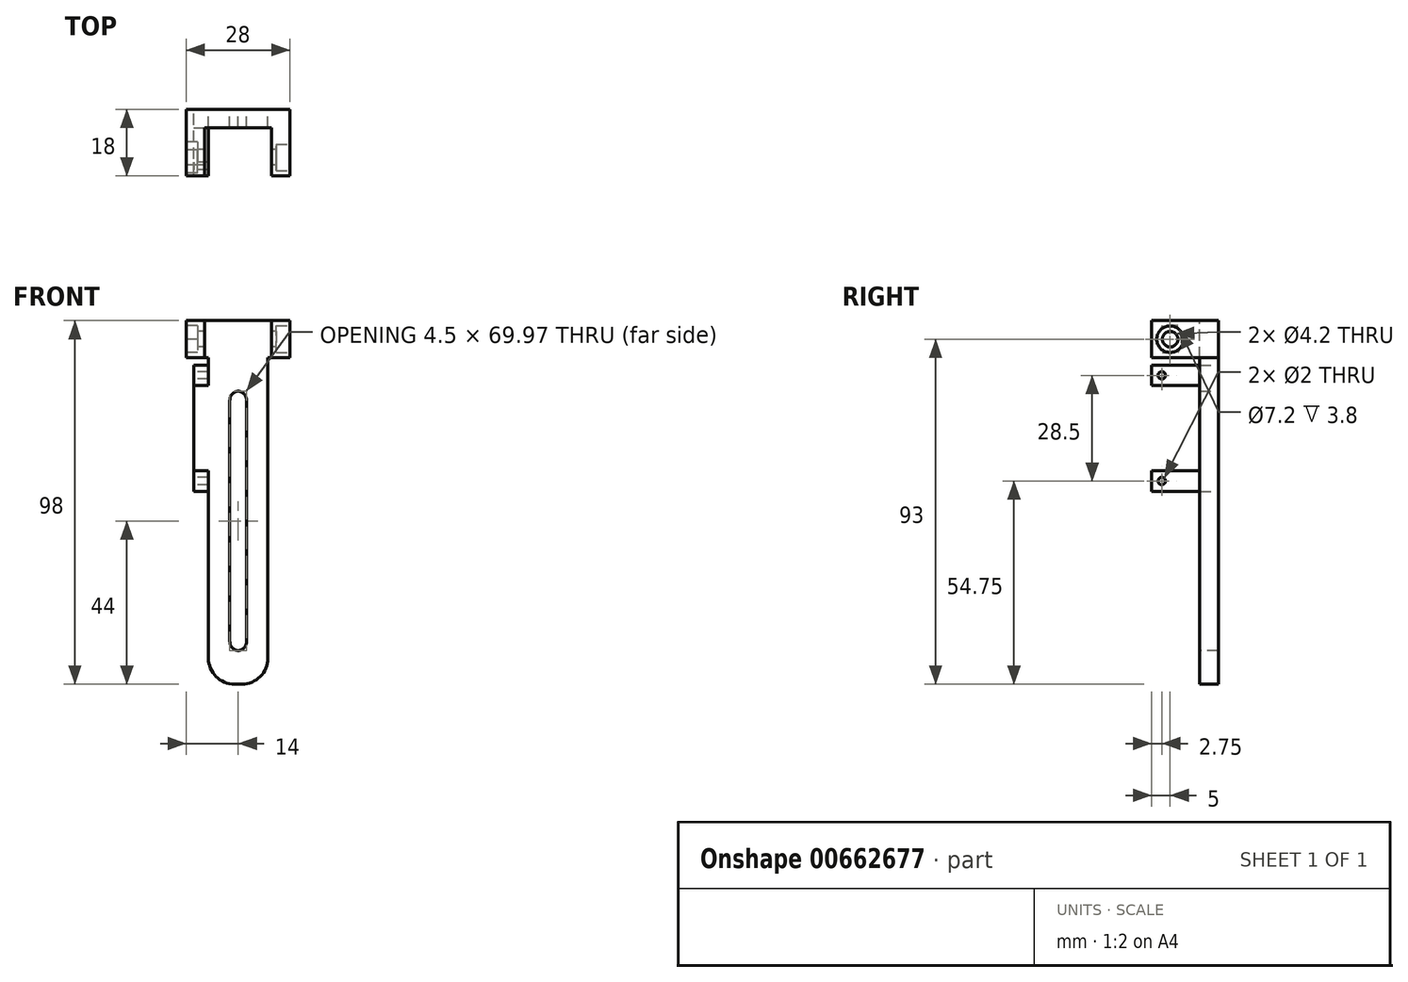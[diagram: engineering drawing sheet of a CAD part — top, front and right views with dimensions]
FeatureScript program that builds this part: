
annotation { "Feature Type Name" : "Feature", "Feature Type Description" : "" }
export const myFeature = defineFeature(function(context is Context, id is Id, definition is map)
    precondition{}
    {
        {
            var Q0;
            Q0=qCreatedBy(makeId("Front.planeOp"),FACE);
            var sketch = newSketch(context, id + "F0", { "sketchPlane" : qUnion([Q0])});
            skLineSegment(sketch, "E0.bottom", {"start": v(8, -44) * mm, "end": v(-8, -44) * mm});
            skLineSegment(sketch, "E0.top", {"start": v(8, 44) * mm, "end": v(-8, 44) * mm});
            skLineSegment(sketch, "E0.left", {"start": v(8, -44) * mm, "end": v(8, 44) * mm});
            skLineSegment(sketch, "E0.right", {"start": v(-8, -44) * mm, "end": v(-8, 44) * mm});
            skPoint(sketch, "E0.middle", {"position": v(0, 0) * mm});
            skLineSegment(sketch, "E1.bottom", {"start": v(-8, 42) * mm, "end": v(-12, 42) * mm});
            skLineSegment(sketch, "E1.top", {"start": v(-8, 8) * mm, "end": v(-12, 8) * mm});
            skLineSegment(sketch, "E1.left", {"start": v(-8, 42) * mm, "end": v(-8, 8) * mm});
            skLineSegment(sketch, "E1.right", {"start": v(-12, 42) * mm, "end": v(-12, 8) * mm});
            skLineSegment(sketch, "E2.bottom", {"start": v(14, 44) * mm, "end": v(8, 44) * mm});
            skLineSegment(sketch, "E2.top", {"start": v(14, 54) * mm, "end": v(-14, 54) * mm});
            skLineSegment(sketch, "E2.left", {"start": v(14, 44) * mm, "end": v(14, 54) * mm});
            skLineSegment(sketch, "E2.right", {"start": v(-14, 44) * mm, "end": v(-14, 54) * mm});
            skLineSegment(sketch, "E3.bottom", {"start": v(2.25, -35) * mm, "end": v(-2.25, -35) * mm});
            skLineSegment(sketch, "E3.top", {"start": v(2.25, 35) * mm, "end": v(-2.25, 35) * mm});
            skLineSegment(sketch, "E3.left", {"start": v(2.25, -35) * mm, "end": v(2.25, 35) * mm});
            skLineSegment(sketch, "E3.right", {"start": v(-2.25, -35) * mm, "end": v(-2.25, 35) * mm});
            skPoint(sketch, "E4", {"position": v(0, 54) * mm});
            skLineSegment(sketch, "E5.trimOffspring", {"start": v(-8, 44) * mm, "end": v(-14, 44) * mm});
            skSolve(sketch);
        }
        {
            var Q0;
            {var subQ1=sQuery(id+"F0.wireOp",EDGE,"E0.bottom");Q0=makeQuery(id+"F0.imprint","IMPRINT",FACE,{"disambiguationData":[TD([[makeQuery(id+"F0.imprint","IMPRINT",EDGE,{"derivedFrom":subQ1}),-1.0]])]});}
            var Q1;
            Q1=makeQuery(id+"F0.imprint","IMPRINT",FACE,{"disambiguationData":[TD([[makeQuery(id+"F0.imprint","IMPRINT",EDGE,{"derivedFrom":sQuery(id+"F0.wireOp",EDGE,"E0.top")}),-1.0]])]});
            var Q2;
            Q2=makeQuery(id+"F0.imprint","IMPRINT",FACE,{"disambiguationData":[TD([[makeQuery(id+"F0.imprint","IMPRINT",EDGE,{"derivedFrom":sQuery(id+"F0.wireOp",EDGE,"E1.bottom")}),1.0]])]});
            extrude(context, id + "F1", {"entities" : qUnion([Q0, Q1, Q2]), "depth" : 5 * mm});
        }
        {
            var Q0;
            Q0=makeQuery(id+"F1.opExtrude","CAP_FACE",FACE,{"disambiguationData":[OSD([sQuery(id+"F0.wireOp",EDGE,"E0.bottom"),sQuery(id+"F0.wireOp",EDGE,"E0.left"),sQuery(id+"F0.wireOp",EDGE,"E0.right"),sQuery(id+"F0.wireOp",EDGE,"E1.bottom"),sQuery(id+"F0.wireOp",EDGE,"E1.top"),sQuery(id+"F0.wireOp",EDGE,"E1.right"),sQuery(id+"F0.wireOp",EDGE,"E2.bottom"),sQuery(id+"F0.wireOp",EDGE,"E2.top"),sQuery(id+"F0.wireOp",EDGE,"E2.left"),sQuery(id+"F0.wireOp",EDGE,"E2.right"),sQuery(id+"F0.wireOp",EDGE,"E3.bottom"),sQuery(id+"F0.wireOp",EDGE,"E3.top"),sQuery(id+"F0.wireOp",EDGE,"E3.left"),sQuery(id+"F0.wireOp",EDGE,"E3.right"),sQuery(id+"F0.wireOp",EDGE,"E5.trimOffspring")])],"isStart":false});
            var sketch = newSketch(context, id + "F2", { "sketchPlane" : qUnion([Q0])});
            skLineSegment(sketch, "E6.bottom", {"start": v(14, 44) * mm, "end": v(9, 44) * mm});
            skLineSegment(sketch, "E6.top", {"start": v(14, 54) * mm, "end": v(9, 54) * mm});
            skLineSegment(sketch, "E6.left", {"start": v(14, 44) * mm, "end": v(14, 54) * mm});
            skLineSegment(sketch, "E6.right", {"start": v(9, 44) * mm, "end": v(9, 54) * mm});
            skLineSegment(sketch, "E7.bottom", {"start": v(-14, 44) * mm, "end": v(-9, 44) * mm});
            skLineSegment(sketch, "E7.top", {"start": v(-14, 54) * mm, "end": v(-9, 54) * mm});
            skLineSegment(sketch, "E7.left", {"start": v(-14, 44) * mm, "end": v(-14, 54) * mm});
            skLineSegment(sketch, "E7.right", {"start": v(-9, 44) * mm, "end": v(-9, 54) * mm});
            skLineSegment(sketch, "E8.bottom", {"start": v(-12, 8) * mm, "end": v(-8, 8) * mm});
            skLineSegment(sketch, "E8.top", {"start": v(-12, 13.5) * mm, "end": v(-8, 13.5) * mm});
            skLineSegment(sketch, "E8.left", {"start": v(-12, 8) * mm, "end": v(-12, 13.5) * mm});
            skLineSegment(sketch, "E8.right", {"start": v(-8, 8) * mm, "end": v(-8, 13.5) * mm});
            skLineSegment(sketch, "E9.bottom", {"start": v(-12, 42) * mm, "end": v(-8, 42) * mm});
            skLineSegment(sketch, "E9.top", {"start": v(-12, 36.5) * mm, "end": v(-8, 36.5) * mm});
            skLineSegment(sketch, "E9.left", {"start": v(-12, 42) * mm, "end": v(-12, 36.5) * mm});
            skLineSegment(sketch, "E9.right", {"start": v(-8, 42) * mm, "end": v(-8, 36.5) * mm});
            skSolve(sketch);
        }
        {
            var Q0;
            Q0=qSketchRegion(id+"F2",true);
            extrude(context, id + "F3", {"entities" : qUnion([Q0]), "operationType" : NewBodyOperationType.ADD, "depth" : 13 * mm});
        }
        {
            var Q0;
            Q0=makeQuery(id+"F3.boolean.opBoolean","MERGE",FACE,{"derivedFrom":[makeQuery(id+"F1.opExtrude","SWEPT_FACE",FACE,{"disambiguationData":[OSD([sQuery(id+"F0.wireOp",EDGE,"E2.right")])]}),makeQuery(id+"F3.opExtrude","SWEPT_FACE",FACE,{"disambiguationData":[OSD([sQuery(id+"F2.wireOp",EDGE,"E7.left")])]})]});
            var sketch = newSketch(context, id + "F4", { "sketchPlane" : qUnion([Q0])});
            skLineSegment(sketch, "E10", {"start": v(0, 49) * mm, "end": v(18, 49) * mm, "construction": true});
            skCircle(sketch, "E11", {"center": v(13, 49) * mm, "radius": 2.1 * mm});
            skLineSegment(sketch, "E12.0.0", {"start": v(0, 42) * mm, "end": v(0, 8) * mm, "construction": true});
            skLineSegment(sketch, "E12.0.1", {"start": v(0, 8) * mm, "end": v(18, 8) * mm, "construction": true});
            skLineSegment(sketch, "E12.0.2", {"start": v(18, 8) * mm, "end": v(18, 13.5) * mm, "construction": true});
            skLineSegment(sketch, "E12.0.3", {"start": v(18, 13.5) * mm, "end": v(5, 13.5) * mm, "construction": true});
            skLineSegment(sketch, "E12.0.4", {"start": v(5, 13.5) * mm, "end": v(5, 36.5) * mm, "construction": true});
            skLineSegment(sketch, "E12.0.5", {"start": v(5, 36.5) * mm, "end": v(18, 36.5) * mm, "construction": true});
            skLineSegment(sketch, "E12.0.6", {"start": v(18, 36.5) * mm, "end": v(18, 42) * mm, "construction": true});
            skLineSegment(sketch, "E12.0.7", {"start": v(18, 42) * mm, "end": v(0, 42) * mm, "construction": true});
            skLineSegment(sketch, "E13", {"start": v(18, 39.25) * mm, "end": v(0, 39.25) * mm, "construction": true});
            skLineSegment(sketch, "E14", {"start": v(18, 10.75) * mm, "end": v(0, 10.75) * mm, "construction": true});
            skCircle(sketch, "E15", {"center": v(15.25, 39.25) * mm, "radius": 1 * mm});
            skCircle(sketch, "E16", {"center": v(15.25, 10.75) * mm, "radius": 1 * mm});
            skSolve(sketch);
        }
        {
            var Q0;
            Q0=makeQuery(id+"F4.imprint","IMPRINT",FACE,{"disambiguationData":[TD([[makeQuery(id+"F4.imprint","IMPRINT",EDGE,{"derivedFrom":sQuery(id+"F4.wireOp",EDGE,"E11")}),1.0]])]});
            var Q1;
            Q1=makeQuery(id+"F4.imprint","IMPRINT",FACE,{"disambiguationData":[TD([[makeQuery(id+"F4.imprint","IMPRINT",EDGE,{"derivedFrom":sQuery(id+"F4.wireOp",EDGE,"E15")}),1.0]])]});
            var Q2;
            Q2=makeQuery(id+"F4.imprint","IMPRINT",FACE,{"disambiguationData":[TD([[makeQuery(id+"F4.imprint","IMPRINT",EDGE,{"derivedFrom":sQuery(id+"F4.wireOp",EDGE,"E16")}),1.0]])]});
            extrude(context, id + "F5", {"entities" : qUnion([Q0, Q1, Q2]), "operationType" : NewBodyOperationType.REMOVE, "endBound" : BoundingType.THROUGH_ALL, "oppositeDirection" : true, "depth" : 25 * mm});
        }
        {
            var Q0;
            Q0=makeQuery(id+"F3.boolean.opBoolean","MERGE",FACE,{"derivedFrom":[makeQuery(id+"F1.opExtrude","SWEPT_FACE",FACE,{"disambiguationData":[OSD([sQuery(id+"F0.wireOp",EDGE,"E2.right")])]}),makeQuery(id+"F3.opExtrude","SWEPT_FACE",FACE,{"disambiguationData":[OSD([sQuery(id+"F2.wireOp",EDGE,"E7.left")])]})]});
            var sketch = newSketch(context, id + "F6", { "sketchPlane" : qUnion([Q0])});
            skCircle(sketch, "E17.cCircle", {"center": v(13, 49) * mm, "radius": 4.16 * mm, "construction": true});
            skPoint(sketch, "E17.cCircle.perimeterSnap0", {"position": v(18, 49) * mm});
            skLineSegment(sketch, "E17.0", {"start": v(17.16, 49) * mm, "end": v(15.08, 45.4) * mm});
            skPoint(sketch, "E17.0.startSnap0", {"position": v(18, 49) * mm});
            skLineSegment(sketch, "E17.1", {"start": v(15.08, 45.4) * mm, "end": v(10.92, 45.4) * mm});
            skLineSegment(sketch, "E17.2", {"start": v(10.92, 45.4) * mm, "end": v(8.84, 49) * mm});
            skLineSegment(sketch, "E17.3", {"start": v(8.84, 49) * mm, "end": v(10.92, 52.6) * mm});
            skLineSegment(sketch, "E17.4", {"start": v(10.92, 52.6) * mm, "end": v(15.08, 52.6) * mm});
            skLineSegment(sketch, "E17.5", {"start": v(15.08, 52.6) * mm, "end": v(17.16, 49) * mm});
            skSolve(sketch);
        }
        {
            var Q0;
            Q0=makeQuery(id+"F6.imprint","IMPRINT",FACE,{"disambiguationData":[TD([[makeQuery(id+"F6.imprint","IMPRINT",EDGE,{"derivedFrom":sQuery(id+"F6.wireOp",EDGE,"E17.0")}),-1.0]])]});
            extrude(context, id + "F7", {"entities" : qUnion([Q0]), "operationType" : NewBodyOperationType.REMOVE, "oppositeDirection" : true, "depth" : 3 * mm});
        }
        {
            var Q0;
            Q0=makeQuery(id+"F3.boolean.opBoolean","MERGE",FACE,{"derivedFrom":[makeQuery(id+"F1.opExtrude","SWEPT_FACE",FACE,{"disambiguationData":[OSD([sQuery(id+"F0.wireOp",EDGE,"E2.left")])]}),makeQuery(id+"F3.opExtrude","SWEPT_FACE",FACE,{"disambiguationData":[OSD([sQuery(id+"F2.wireOp",EDGE,"E6.left")])]})]});
            var sketch = newSketch(context, id + "F8", { "sketchPlane" : qUnion([Q0])});
            skCircle(sketch, "E18", {"center": v(-13, 49) * mm, "radius": 3.6 * mm});
            skSolve(sketch);
        }
        {
            var Q0;
            Q0=makeQuery(id+"F8.imprint","IMPRINT",FACE,{"disambiguationData":[TD([[makeQuery(id+"F8.imprint","IMPRINT",EDGE,{"derivedFrom":sQuery(id+"F8.wireOp",EDGE,"E18")}),1.0]])]});
            extrude(context, id + "F9", {"entities" : qUnion([Q0]), "operationType" : NewBodyOperationType.REMOVE, "oppositeDirection" : true, "depth" : 3.8 * mm});
        }
        {
            var Q0;
            Q0=makeQuery(id+"F1.opExtrude","SWEPT_EDGE",EDGE,{"disambiguationData":[OSD([sQuery(id+"F0.wireOp",EDGE,"E0.bottom"),sQuery(id+"F0.wireOp",EDGE,"E0.left")])]});
            var Q1;
            Q1=makeQuery(id+"F1.opExtrude","SWEPT_EDGE",EDGE,{"disambiguationData":[OSD([sQuery(id+"F0.wireOp",EDGE,"E0.bottom"),sQuery(id+"F0.wireOp",EDGE,"E0.right")])]});
            fillet(context, id + "F10", {"entities" : qUnion([Q0, Q1]), "radius" : 7 * mm, "tangentPropagation" : true, "allowEdgeOverflow" : false});
        }
        {
            var Q0;
            Q0=makeQuery(id+"F1.opExtrude","SWEPT_EDGE",EDGE,{"disambiguationData":[OSD([sQuery(id+"F0.wireOp",EDGE,"E3.bottom"),sQuery(id+"F0.wireOp",EDGE,"E3.right")])]});
            var Q1;
            Q1=makeQuery(id+"F1.opExtrude","SWEPT_EDGE",EDGE,{"disambiguationData":[OSD([sQuery(id+"F0.wireOp",EDGE,"E3.bottom"),sQuery(id+"F0.wireOp",EDGE,"E3.left")])]});
            var Q2;
            Q2=makeQuery(id+"F1.opExtrude","SWEPT_EDGE",EDGE,{"disambiguationData":[OSD([sQuery(id+"F0.wireOp",EDGE,"E3.top"),sQuery(id+"F0.wireOp",EDGE,"E3.right")])]});
            var Q3;
            Q3=makeQuery(id+"F1.opExtrude","SWEPT_EDGE",EDGE,{"disambiguationData":[OSD([sQuery(id+"F0.wireOp",EDGE,"E3.top"),sQuery(id+"F0.wireOp",EDGE,"E3.left")])]});
            fillet(context, id + "F11", {"entities" : qUnion([Q0, Q1, Q2, Q3]), "radius" : 2.5 * mm, "tangentPropagation" : true, "allowEdgeOverflow" : false});
        }
    });
